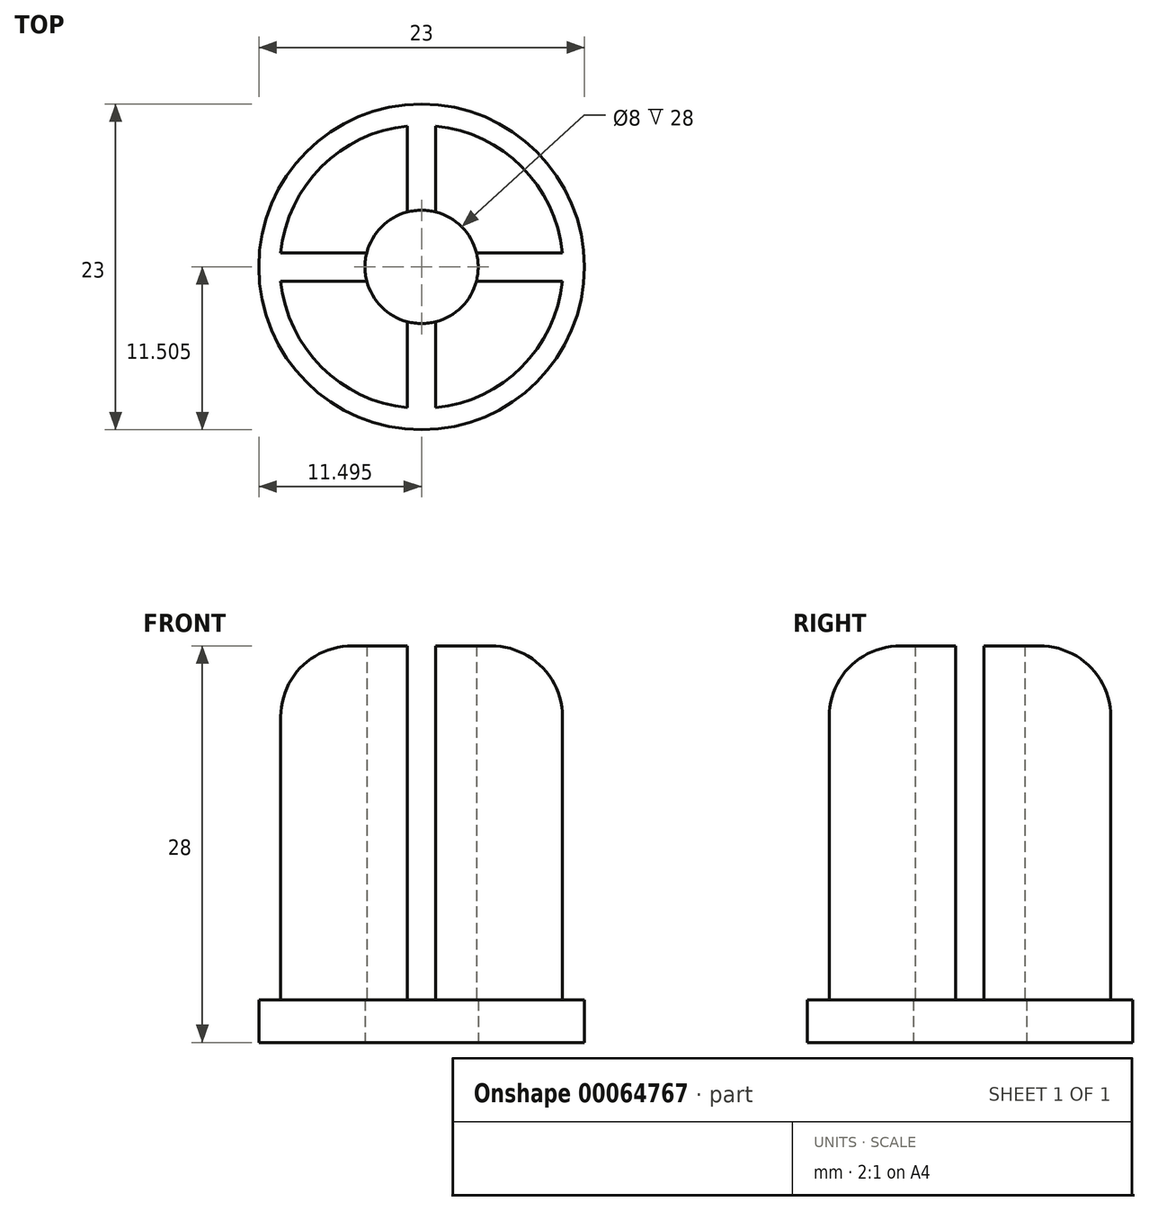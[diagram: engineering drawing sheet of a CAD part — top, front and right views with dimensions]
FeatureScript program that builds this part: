
annotation { "Feature Type Name" : "Feature", "Feature Type Description" : "" }
export const myFeature = defineFeature(function(context is Context, id is Id, definition is map)
    precondition{}
    {
        {
            var Q0;
            Q0=qCreatedBy(makeId("Top.planeOp"),FACE);
            var sketch = newSketch(context, id + "F0", { "sketchPlane" : qUnion([Q0])});
            skCircle(sketch, "E0", {"center": v(0, 0) * mm, "radius": 10 * mm});
            skCircle(sketch, "E1", {"center": v(0, 0) * mm, "radius": 4 * mm});
            skSolve(sketch);
        }
        {
            var Q0;
            Q0=qSketchRegion(id+"F0",true);
            extrude(context, id + "F1", {"entities" : qUnion([Q0]), "depth" : 25 * mm});
        }
        {
            var Q0;
            Q0=qCreatedBy(makeId("Top.planeOp"),FACE);
            var sketch = newSketch(context, id + "F2", { "sketchPlane" : qUnion([Q0])});
            skCircle(sketch, "E2", {"center": v(0, 0) * mm, "radius": 11.5 * mm});
            skCircle(sketch, "E3", {"center": v(0, 0) * mm, "radius": 4 * mm});
            skSolve(sketch);
        }
        {
            var Q0;
            Q0=qSketchRegion(id+"F2",true);
            extrude(context, id + "F3", {"entities" : qUnion([Q0]), "operationType" : NewBodyOperationType.ADD, "oppositeDirection" : true, "depth" : 3 * mm});
        }
        {
            var Q0;
            Q0=qCreatedBy(makeId("Top.planeOp"),FACE);
            var sketch = newSketch(context, id + "F4", { "sketchPlane" : qUnion([Q0])});
            skLineSegment(sketch, "E4.top", {"start": v(-16.4, 1) * mm, "end": v(17.64, 1) * mm});
            skLineSegment(sketch, "E5.top", {"start": v(-16.4, -1) * mm, "end": v(18.02, -1) * mm});
            skLineSegment(sketch, "E6.right", {"start": v(-1, 15.85) * mm, "end": v(-1, -19.36) * mm});
            skLineSegment(sketch, "E7.right", {"start": v(1, 15.85) * mm, "end": v(1, -19.36) * mm});
            skLineSegment(sketch, "E8", {"start": v(-1, 15.85) * mm, "end": v(1, 15.85) * mm});
            skLineSegment(sketch, "E9", {"start": v(-16.4, 1) * mm, "end": v(-16.4, -1) * mm});
            skLineSegment(sketch, "E10", {"start": v(17.64, 1) * mm, "end": v(18.02, -1) * mm});
            skLineSegment(sketch, "E11", {"start": v(-1, -19.36) * mm, "end": v(1, -19.36) * mm});
            skSolve(sketch);
        }
        {
            var Q0;
            Q0=qSketchRegion(id+"F4",true);
            extrude(context, id + "F5", {"entities" : qUnion([Q0]), "operationType" : NewBodyOperationType.REMOVE, "depth" : 25 * mm});
        }
        {
            var Q0;
            {var subQ0=sQuery(id+"F0.wireOp",EDGE,"E0");var subQ2=sQuery(id+"F4.wireOp",EDGE,"E5.top");Q0=makeQuery(id+"F5.boolean.opBoolean","SPLIT",EDGE,{"disambiguationData":[TD([makeQuery(id+"F5.opExtrude","SWEPT_FACE",FACE,{"disambiguationData":[OSD([subQ2]),TDD([makeQuery(id+"F4.imprint","IMPRINT",EDGE,{"disambiguationData":[TD([[makeQuery(id+"F4.imprint","INTERSECT",VERTEX,{"derivedFrom":[subQ2,sQuery(id+"F4.wireOp",EDGE,"E10")]}),1.0]])],"derivedFrom":subQ2})])]})])],"derivedFrom":makeQuery(id+"F1.opExtrude","CAP_EDGE",EDGE,{"disambiguationData":[OSD([subQ0])],"isStart":false})});}
            var Q1;
            {var subQ0=sQuery(id+"F0.wireOp",EDGE,"E0");var subQ2=sQuery(id+"F4.wireOp",EDGE,"E4.top");Q1=makeQuery(id+"F5.boolean.opBoolean","SPLIT",EDGE,{"disambiguationData":[TD([makeQuery(id+"F5.opExtrude","SWEPT_FACE",FACE,{"disambiguationData":[OSD([subQ2]),TDD([makeQuery(id+"F4.imprint","IMPRINT",EDGE,{"disambiguationData":[TD([[makeQuery(id+"F4.imprint","INTERSECT",VERTEX,{"derivedFrom":[subQ2,sQuery(id+"F4.wireOp",EDGE,"E10")]}),1.0]])],"derivedFrom":subQ2})])]})])],"derivedFrom":makeQuery(id+"F1.opExtrude","CAP_EDGE",EDGE,{"disambiguationData":[OSD([subQ0])],"isStart":false})});}
            var Q2;
            {var subQ0=sQuery(id+"F0.wireOp",EDGE,"E0");var subQ2=sQuery(id+"F4.wireOp",EDGE,"E4.top");Q2=makeQuery(id+"F5.boolean.opBoolean","SPLIT",EDGE,{"disambiguationData":[TD([makeQuery(id+"F5.opExtrude","SWEPT_FACE",FACE,{"disambiguationData":[OSD([subQ2]),TDD([makeQuery(id+"F4.imprint","IMPRINT",EDGE,{"disambiguationData":[TD([[makeQuery(id+"F4.imprint","INTERSECT",VERTEX,{"derivedFrom":[subQ2,sQuery(id+"F4.wireOp",EDGE,"E9")]}),-1.0]])],"derivedFrom":subQ2})])]})])],"derivedFrom":makeQuery(id+"F1.opExtrude","CAP_EDGE",EDGE,{"disambiguationData":[OSD([subQ0])],"isStart":false})});}
            var Q3;
            {var subQ0=sQuery(id+"F0.wireOp",EDGE,"E0");var subQ2=sQuery(id+"F4.wireOp",EDGE,"E5.top");Q3=makeQuery(id+"F5.boolean.opBoolean","SPLIT",EDGE,{"disambiguationData":[TD([makeQuery(id+"F5.opExtrude","SWEPT_FACE",FACE,{"disambiguationData":[OSD([subQ2]),TDD([makeQuery(id+"F4.imprint","IMPRINT",EDGE,{"disambiguationData":[TD([[makeQuery(id+"F4.imprint","INTERSECT",VERTEX,{"derivedFrom":[subQ2,sQuery(id+"F4.wireOp",EDGE,"E9")]}),-1.0]])],"derivedFrom":subQ2})])]})])],"derivedFrom":makeQuery(id+"F1.opExtrude","CAP_EDGE",EDGE,{"disambiguationData":[OSD([subQ0])],"isStart":false})});}
            fillet(context, id + "F6", {"entities" : qUnion([Q0, Q1, Q2, Q3]), "radius" : 5 * mm, "tangentPropagation" : true, "allowEdgeOverflow" : false});
        }
        {
            var Q0;
            Q0=qCreatedBy(makeId("Top.planeOp"),FACE);
            var sketch = newSketch(context, id + "F7", { "sketchPlane" : qUnion([Q0])});
            skLineSegment(sketch, "E12.bottom", {"start": v(-110.46, -34.24) * mm, "end": v(-55.47, -34.24) * mm});
            skLineSegment(sketch, "E12.top", {"start": v(-110.46, -79.48) * mm, "end": v(-55.47, -79.48) * mm});
            skLineSegment(sketch, "E12.left", {"start": v(-110.46, -34.24) * mm, "end": v(-110.46, -79.48) * mm});
            skLineSegment(sketch, "E12.right", {"start": v(-55.47, -34.24) * mm, "end": v(-55.47, -79.48) * mm});
            skSolve(sketch);
        }
        {
            var Q0;
            Q0=qSketchRegion(id+"F7",true);
            extrude(context, id + "F8", {"entities" : qUnion([Q0]), "depth" : 25 * mm});
        }
        {
            var Q0;
            Q0=makeQuery(id+"F8.opExtrude","SWEPT_BODY",BODY,{"disambiguationData":[OSD([sQuery(id+"F7.wireOp",EDGE,"E12.bottom"),sQuery(id+"F7.wireOp",EDGE,"E12.top"),sQuery(id+"F7.wireOp",EDGE,"E12.left"),sQuery(id+"F7.wireOp",EDGE,"E12.right")])]});
            deleteBodies(context, id + "F9", {"entities" : qUnion([Q0])});
        }
        {
            var Q0;
            Q0=qCreatedBy(makeId("Right.planeOp"),FACE);
            var sketch = newSketch(context, id + "F10", { "sketchPlane" : qUnion([Q0])});
            skLineSegment(sketch, "E13", {"start": v(-20.04, 51.85) * mm, "end": v(-20.04, -35.71) * mm, "construction": true});
            skSolve(sketch);
        }
        {
            var Q0;
            {var subQ0=sQuery(id+"F0.wireOp",EDGE,"E0");var subQ2=sQuery(id+"F4.wireOp",EDGE,"E4.top");var subQ5=sQuery(id+"F4.wireOp",EDGE,"E10");Q0=makeQuery(id+"F5.boolean.opBoolean","SPLIT",FACE,{"disambiguationData":[TD([makeQuery(id+"F5.opExtrude","SWEPT_FACE",FACE,{"disambiguationData":[OSD([subQ2]),TDD([makeQuery(id+"F4.imprint","IMPRINT",EDGE,{"disambiguationData":[TD([[makeQuery(id+"F4.imprint","INTERSECT",VERTEX,{"derivedFrom":[subQ2,subQ5]}),1.0]])],"derivedFrom":subQ2})])]})])],"derivedFrom":makeQuery(id+"F1.opExtrude","SWEPT_FACE",FACE,{"disambiguationData":[OSD([subQ0])]})});}
            var Q1;
            Q1=makeQuery(id+"F1.opExtrude","SWEPT_BODY",BODY,{"disambiguationData":[OSD([sQuery(id+"F0.wireOp",EDGE,"E0"),sQuery(id+"F0.wireOp",EDGE,"E1")])]});
            var Q2;
            Q2=sQuery(id+"F10.wireOp",EDGE,"E13");
            circularPattern(context, id + "F11", {"entities" : qUnion([Q1]), "axis" : qUnion([Q2]), "angle" : 90 * degree, "instanceCount" : round(4)});
        }
        {
            var Q0;
            Q0=makeQuery(id+"F1.opExtrude","SWEPT_BODY",BODY,{"disambiguationData":[OSD([sQuery(id+"F0.wireOp",EDGE,"E0"),sQuery(id+"F0.wireOp",EDGE,"E1")])]});
            deleteBodies(context, id + "F12", {"entities" : qUnion([Q0])});
        }
        {
            var Q0;
            Q0=makeQuery(id+"F11.opPattern","COPY",BODY,{"derivedFrom":makeQuery(id+"F1.opExtrude","SWEPT_BODY",BODY,{"disambiguationData":[OSD([sQuery(id+"F0.wireOp",EDGE,"E0"),sQuery(id+"F0.wireOp",EDGE,"E1")])]}),"instanceName":"2"});
            deleteBodies(context, id + "F13", {"entities" : qUnion([Q0])});
        }
        {
            var Q0;
            Q0=makeQuery(id+"F11.opPattern","COPY",BODY,{"derivedFrom":makeQuery(id+"F1.opExtrude","SWEPT_BODY",BODY,{"disambiguationData":[OSD([sQuery(id+"F0.wireOp",EDGE,"E0"),sQuery(id+"F0.wireOp",EDGE,"E1")])]}),"instanceName":"3"});
            deleteBodies(context, id + "F14", {"entities" : qUnion([Q0])});
        }
    });
